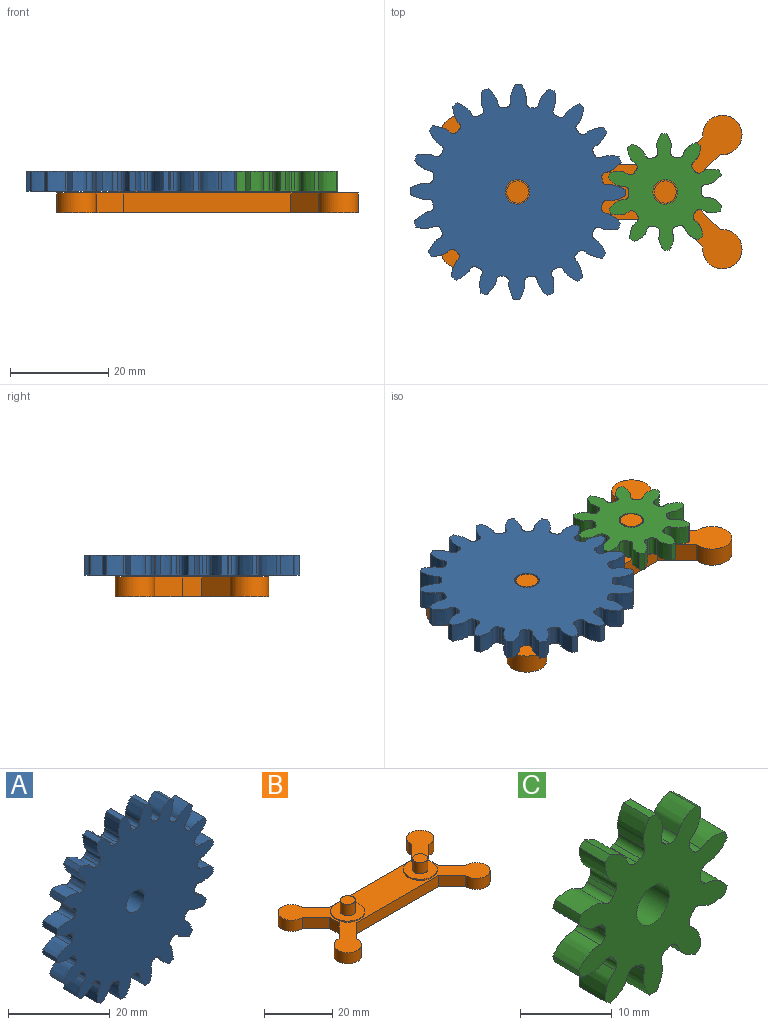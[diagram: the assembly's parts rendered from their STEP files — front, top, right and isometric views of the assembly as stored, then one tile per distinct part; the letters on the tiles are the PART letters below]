
ASSEMBLY  parts=3 mates=2
PART A: 123 faces, bbox 43.9x4.5x43.9 mm
  f0: cylinder r=21.88mm len=4mm, axis (0,1,0), area 5mm2, adj f19,f22,f73,f120
  f1: cylinder r=21.88mm len=4mm, axis (0,1,0), area 5mm2, adj f19,f22,f115,f118
  f2: cylinder r=21.88mm len=4mm, axis (0,1,0), area 5mm2, adj f19,f22,f110,f113
  f3: cylinder r=21.88mm len=4mm, axis (0,1,0), area 5mm2, adj f19,f22,f105,f108
  f4: cylinder r=21.88mm len=4mm, axis (0,1,0), area 5mm2, adj f19,f22,f100,f103
  f5: cylinder r=21.88mm len=4mm, axis (0,1,0), area 5mm2, adj f19,f22,f95,f98
  f6: cylinder r=21.88mm len=4mm, axis (0,1,0), area 5mm2, adj f19,f22,f90,f93
  f7: cylinder r=21.88mm len=4mm, axis (0,1,0), area 5mm2, adj f19,f22,f85,f88
  f8: cylinder r=21.88mm len=4mm, axis (0,1,0), area 5mm2, adj f19,f22,f68,f80
  f9: cylinder r=21.88mm len=4mm, axis (0,1,0), area 5mm2, adj f19,f22,f75,f78
  f10: cylinder r=21.88mm len=4mm, axis (0,1,0), area 5mm2, adj f19,f22,f63,f70
  f11: cylinder r=21.88mm len=4mm, axis (0,1,0), area 5mm2, adj f19,f22,f43,f65
  f12: cylinder r=21.88mm len=4mm, axis (0,1,0), area 5mm2, adj f19,f22,f23,f60
  f13: cylinder r=21.88mm len=4mm, axis (0,1,0), area 5mm2, adj f19,f22,f55,f58
  f14: cylinder r=21.88mm len=4mm, axis (0,1,0), area 5mm2, adj f19,f22,f50,f53
  f15: cylinder r=21.88mm len=4mm, axis (0,1,0), area 5mm2, adj f19,f22,f45,f48
  f16: cylinder r=21.88mm len=4mm, axis (0,1,0), area 5mm2, adj f19,f22,f33,f40
  f17: cylinder r=21.88mm len=4mm, axis (0,1,0), area 5mm2, adj f19,f22,f35,f83
  f18: cylinder r=21.88mm len=4mm, axis (0,1,0), area 5mm2, adj f19,f22,f30,f38
  f19: plane 43.87x43.87mm, normal (0,-1,0), area 1180.5mm2, adj f0,f1,f2,f3,f4,f5,f6,f7
  f20: cylinder r=2.5mm len=5mm, axis (0,1,0), area 62.8mm2, adj f19,f22
  f21: cylinder r=21.88mm len=4mm, axis (0,1,0), area 5mm2, adj f19,f22,f25,f28
  f22: plane 43.87x43.87mm, normal (0,1,0), area 1180.5mm2, adj f0,f1,f2,f3,f4,f5,f6,f7
  f23: extruded ~4x3.46mm, area 15.4mm2, adj f12,f19,f22,f26
  f24: cylinder r=17.38mm len=4mm, axis (0,1,0), area 2.8mm2, adj f19,f22,f26,f27
  f25: extruded ~4x3.46mm, area 15.4mm2, adj f19,f21,f22,f27
  f26: cylinder r=0.92mm len=4mm, axis (0,1,0), area 5.6mm2, adj f19,f22,f23,f24
  f27: cylinder r=0.92mm len=4mm, axis (0,1,0), area 5.6mm2, adj f19,f22,f24,f25
  f28: extruded ~4x3.77mm, area 15.4mm2, adj f19,f21,f22,f31
  f29: cylinder r=17.38mm len=4mm, axis (0,1,0), area 2.8mm2, adj f19,f22,f31,f32
  f30: extruded ~4x2.82mm, area 15.4mm2, adj f18,f19,f22,f32
  f31: cylinder r=0.92mm len=4mm, axis (0,1,0), area 5.6mm2, adj f19,f22,f28,f29
  f32: cylinder r=0.92mm len=4mm, axis (0,1,0), area 5.6mm2, adj f19,f22,f29,f30
  f33: extruded ~4x3.27mm, area 15.4mm2, adj f16,f19,f22,f36
  f34: cylinder r=17.38mm len=4mm, axis (0,1,0), area 2.8mm2, adj f19,f22,f36,f37
  f35: extruded ~4x3.7mm, area 15.4mm2, adj f17,f19,f22,f37
  f36: cylinder r=0.92mm len=4mm, axis (0,1,0), area 5.6mm2, adj f19,f22,f33,f34
  f37: cylinder r=0.92mm len=4mm, axis (0,1,0), area 5.6mm2, adj f19,f22,f34,f35
  f38: extruded ~4x3.7mm, area 15.4mm2, adj f18,f19,f22,f41
  f39: cylinder r=17.38mm len=4mm, axis (0,1,0), area 2.8mm2, adj f19,f22,f41,f42
  f40: extruded ~4x3.27mm, area 15.4mm2, adj f16,f19,f22,f42
  f41: cylinder r=0.92mm len=4mm, axis (0,1,0), area 5.6mm2, adj f19,f22,f38,f39
  f42: cylinder r=0.92mm len=4mm, axis (0,1,0), area 5.6mm2, adj f19,f22,f39,f40
  f43: extruded ~4x3.77mm, area 15.4mm2, adj f11,f19,f22,f46
  f44: cylinder r=17.38mm len=4mm, axis (0,1,0), area 2.8mm2, adj f19,f22,f46,f47
  f45: extruded ~4x2.82mm, area 15.4mm2, adj f15,f19,f22,f47
  f46: cylinder r=0.92mm len=4mm, axis (0,1,0), area 5.6mm2, adj f19,f22,f43,f44
  f47: cylinder r=0.92mm len=4mm, axis (0,1,0), area 5.6mm2, adj f19,f22,f44,f45
  f48: extruded ~4x3.7mm, area 15.4mm2, adj f15,f19,f22,f51
  f49: cylinder r=17.38mm len=4mm, axis (0,1,0), area 2.8mm2, adj f19,f22,f51,f52
  f50: extruded ~4x3.27mm, area 15.4mm2, adj f14,f19,f22,f52
  f51: cylinder r=0.92mm len=4mm, axis (0,1,0), area 5.6mm2, adj f19,f22,f48,f49
  f52: cylinder r=0.92mm len=4mm, axis (0,1,0), area 5.6mm2, adj f19,f22,f49,f50
  f53: extruded ~4x3.27mm, area 15.4mm2, adj f14,f19,f22,f56
  f54: cylinder r=17.38mm len=4mm, axis (0,1,0), area 2.8mm2, adj f19,f22,f56,f57
  f55: extruded ~4x3.7mm, area 15.4mm2, adj f13,f19,f22,f57
  f56: cylinder r=0.92mm len=4mm, axis (0,1,0), area 5.6mm2, adj f19,f22,f53,f54
  f57: cylinder r=0.92mm len=4mm, axis (0,1,0), area 5.6mm2, adj f19,f22,f54,f55
  f58: extruded ~4x2.82mm, area 15.4mm2, adj f13,f19,f22,f61
  f59: cylinder r=17.38mm len=4mm, axis (0,1,0), area 2.8mm2, adj f19,f22,f61,f62
  f60: extruded ~4x3.77mm, area 15.4mm2, adj f12,f19,f22,f62
  f61: cylinder r=0.92mm len=4mm, axis (0,1,0), area 5.6mm2, adj f19,f22,f58,f59
  f62: cylinder r=0.92mm len=4mm, axis (0,1,0), area 5.6mm2, adj f19,f22,f59,f60
  f63: extruded ~4x3.46mm, area 15.4mm2, adj f10,f19,f22,f66
  f64: cylinder r=17.38mm len=4mm, axis (0,1,0), area 2.8mm2, adj f19,f22,f66,f67
  f65: extruded ~4x3.46mm, area 15.4mm2, adj f11,f19,f22,f67
  f66: cylinder r=0.92mm len=4mm, axis (0,1,0), area 5.6mm2, adj f19,f22,f63,f64
  f67: cylinder r=0.92mm len=4mm, axis (0,1,0), area 5.6mm2, adj f19,f22,f64,f65
  f68: extruded ~4x2.82mm, area 15.4mm2, adj f8,f19,f22,f71
  f69: cylinder r=17.38mm len=4mm, axis (0,1,0), area 2.8mm2, adj f19,f22,f71,f72
  f70: extruded ~4x3.77mm, area 15.4mm2, adj f10,f19,f22,f72
  f71: cylinder r=0.92mm len=4mm, axis (0,1,0), area 5.6mm2, adj f19,f22,f68,f69
  f72: cylinder r=0.92mm len=4mm, axis (0,1,0), area 5.6mm2, adj f19,f22,f69,f70
  f73: extruded ~4x3.7mm, area 15.4mm2, adj f0,f19,f22,f76
  f74: cylinder r=17.38mm len=4mm, axis (0,1,0), area 2.8mm2, adj f19,f22,f76,f77
  f75: extruded ~4x3.27mm, area 15.4mm2, adj f9,f19,f22,f77
  f76: cylinder r=0.92mm len=4mm, axis (0,1,0), area 5.6mm2, adj f19,f22,f73,f74
  f77: cylinder r=0.92mm len=4mm, axis (0,1,0), area 5.6mm2, adj f19,f22,f74,f75
  f78: extruded ~4x3.27mm, area 15.4mm2, adj f9,f19,f22,f81
  f79: cylinder r=17.38mm len=4mm, axis (0,1,0), area 2.8mm2, adj f19,f22,f81,f82
  f80: extruded ~4x3.7mm, area 15.4mm2, adj f8,f19,f22,f82
  f81: cylinder r=0.92mm len=4mm, axis (0,1,0), area 5.6mm2, adj f19,f22,f78,f79
  f82: cylinder r=0.92mm len=4mm, axis (0,1,0), area 5.6mm2, adj f19,f22,f79,f80
  f83: extruded ~4x2.82mm, area 15.4mm2, adj f17,f19,f22,f86
  f84: cylinder r=17.38mm len=4mm, axis (0,1,0), area 2.8mm2, adj f19,f22,f86,f87
  f85: extruded ~4x3.77mm, area 15.4mm2, adj f7,f19,f22,f87
  f86: cylinder r=0.92mm len=4mm, axis (0,1,0), area 5.6mm2, adj f19,f22,f83,f84
  f87: cylinder r=0.92mm len=4mm, axis (0,1,0), area 5.6mm2, adj f19,f22,f84,f85
  f88: extruded ~4x3.46mm, area 15.4mm2, adj f7,f19,f22,f91
  f89: cylinder r=17.38mm len=4mm, axis (0,1,0), area 2.8mm2, adj f19,f22,f91,f92
  f90: extruded ~4x3.46mm, area 15.4mm2, adj f6,f19,f22,f92
  f91: cylinder r=0.92mm len=4mm, axis (0,1,0), area 5.6mm2, adj f19,f22,f88,f89
  f92: cylinder r=0.92mm len=4mm, axis (0,1,0), area 5.6mm2, adj f19,f22,f89,f90
  f93: extruded ~4x3.77mm, area 15.4mm2, adj f6,f19,f22,f96
  f94: cylinder r=17.38mm len=4mm, axis (0,1,0), area 2.8mm2, adj f19,f22,f96,f97
  f95: extruded ~4x2.82mm, area 15.4mm2, adj f5,f19,f22,f97
  f96: cylinder r=0.92mm len=4mm, axis (0,1,0), area 5.6mm2, adj f19,f22,f93,f94
  f97: cylinder r=0.92mm len=4mm, axis (0,1,0), area 5.6mm2, adj f19,f22,f94,f95
  f98: extruded ~4x3.7mm, area 15.4mm2, adj f5,f19,f22,f101
  f99: cylinder r=17.38mm len=4mm, axis (0,1,0), area 2.8mm2, adj f19,f22,f101,f102
  f100: extruded ~4x3.27mm, area 15.4mm2, adj f4,f19,f22,f102
  f101: cylinder r=0.92mm len=4mm, axis (0,1,0), area 5.6mm2, adj f19,f22,f98,f99
  f102: cylinder r=0.92mm len=4mm, axis (0,1,0), area 5.6mm2, adj f19,f22,f99,f100
  f103: extruded ~4x3.27mm, area 15.4mm2, adj f4,f19,f22,f106
  f104: cylinder r=17.38mm len=4mm, axis (0,1,0), area 2.8mm2, adj f19,f22,f106,f107
  f105: extruded ~4x3.7mm, area 15.4mm2, adj f3,f19,f22,f107
  f106: cylinder r=0.92mm len=4mm, axis (0,1,0), area 5.6mm2, adj f19,f22,f103,f104
  f107: cylinder r=0.92mm len=4mm, axis (0,1,0), area 5.6mm2, adj f19,f22,f104,f105
  f108: extruded ~4x2.82mm, area 15.4mm2, adj f3,f19,f22,f111
  f109: cylinder r=17.38mm len=4mm, axis (0,1,0), area 2.8mm2, adj f19,f22,f111,f112
  f110: extruded ~4x3.77mm, area 15.4mm2, adj f2,f19,f22,f112
  f111: cylinder r=0.92mm len=4mm, axis (0,1,0), area 5.6mm2, adj f19,f22,f108,f109
  f112: cylinder r=0.92mm len=4mm, axis (0,1,0), area 5.6mm2, adj f19,f22,f109,f110
  f113: extruded ~4x3.46mm, area 15.4mm2, adj f2,f19,f22,f116
  f114: cylinder r=17.38mm len=4mm, axis (0,1,0), area 2.8mm2, adj f19,f22,f116,f117
  f115: extruded ~4x3.46mm, area 15.4mm2, adj f1,f19,f22,f117
  f116: cylinder r=0.92mm len=4mm, axis (0,1,0), area 5.6mm2, adj f19,f22,f113,f114
  f117: cylinder r=0.92mm len=4mm, axis (0,1,0), area 5.6mm2, adj f19,f22,f114,f115
  f118: extruded ~4x3.77mm, area 15.4mm2, adj f1,f19,f22,f121
  f119: cylinder r=17.38mm len=4mm, axis (0,1,0), area 2.8mm2, adj f19,f22,f121,f122
  f120: extruded ~4x2.82mm, area 15.4mm2, adj f0,f19,f22,f122
  f121: cylinder r=0.92mm len=4mm, axis (0,1,0), area 5.6mm2, adj f19,f22,f118,f119
  f122: cylinder r=0.92mm len=4mm, axis (0,1,0), area 5.6mm2, adj f19,f22,f119,f120
PART B: 26 faces, bbox 61.3x31.2x8.4 mm
  f0: cylinder r=4mm len=8mm, axis (0,0,1), area 78.9mm2, adj f1,f15,f16,f17
  f1: plane 5.66x5.66mm, normal (-0.71,0.71,0), area 32mm2, adj f0,f2,f16,f17
  f2: plane 34x4mm, normal (0,1,0), area 136mm2, adj f1,f3,f16,f17
  f3: plane 5.66x5.66mm, normal (0.71,0.71,0), area 32mm2, adj f2,f4,f16,f17
  f4: cylinder r=4mm len=8mm, axis (0,0,1), area 78.9mm2, adj f3,f5,f16,f17
  f5: plane 5.66x5.66mm, normal (-0.71,-0.71,0), area 32mm2, adj f4,f6,f16,f17
  f6: plane 4x3.93mm, normal (-1,0,0), area 15.7mm2, adj f5,f7,f16,f17
  f7: plane 5.66x5.66mm, normal (-0.71,0.71,0), area 32mm2, adj f6,f8,f16,f17
  f8: cylinder r=4mm len=8mm, axis (0,0,1), area 78.9mm2, adj f7,f9,f16,f17
  f9: plane 5.66x5.66mm, normal (0.71,-0.71,0), area 32mm2, adj f8,f10,f16,f17
  f10: plane 34x4mm, normal (0,-1,0), area 136mm2, adj f9,f11,f16,f17
  f11: plane 5.66x5.66mm, normal (-0.71,-0.71,0), area 32mm2, adj f10,f12,f16,f17
  f12: cylinder r=4mm len=8mm, axis (0,0,1), area 78.9mm2, adj f11,f13,f16,f17
  f13: plane 5.66x5.66mm, normal (0.71,0.71,0), area 32mm2, adj f12,f14,f16,f17
  f14: plane 4x3.93mm, normal (1,0,0), area 15.7mm2, adj f13,f15,f16,f17
  f15: plane 5.66x5.66mm, normal (0.71,-0.71,0), area 32mm2, adj f0,f14,f16,f17
  f16: plane 61.27x31.19mm, normal (0,0,-1), area 775.9mm2, adj f0,f1,f2,f3,f4,f5,f6,f7
  f17: plane 61.27x31.19mm, normal (0,0,1), area 618.8mm2, adj f0,f1,f2,f3,f4,f5,f6,f7
  f18: cylinder r=5mm len=10mm, axis (0,0,-1), area 12.6mm2, adj f17,f19
  f19: plane 10x10mm, normal (0,0,1), area 62.6mm2, adj f18,f21
  f20: plane 4.5x4.5mm, normal (0,0,1), area 15.9mm2, adj f21
  f21: cylinder r=2.25mm len=4.5mm, axis (0,0,-1), area 56.5mm2, adj f19,f20
  f22: cylinder r=5mm len=10mm, axis (0,0,-1), area 12.6mm2, adj f17,f23
  f23: plane 10x10mm, normal (0,0,1), area 62.6mm2, adj f22,f25
  f24: plane 4.5x4.5mm, normal (0,0,1), area 15.9mm2, adj f25
  f25: cylinder r=2.25mm len=4.5mm, axis (0,0,-1), area 56.5mm2, adj f23,f24
PART C: 63 faces, bbox 24.1x5.2x24.9 mm
  f0: cylinder r=11.88mm len=4mm, axis (0,1,0), area 4.2mm2, adj f9,f12,f53,f60
  f1: cylinder r=11.88mm len=4mm, axis (0,1,0), area 4.2mm2, adj f9,f12,f13,f55
  f2: cylinder r=11.88mm len=4mm, axis (0,1,0), area 4.2mm2, adj f9,f12,f43,f50
  f3: cylinder r=11.88mm len=4mm, axis (0,1,0), area 4.2mm2, adj f9,f12,f45,f58
  f4: cylinder r=11.88mm len=4mm, axis (0,1,0), area 4.2mm2, adj f9,f12,f33,f40
  f5: cylinder r=11.88mm len=4mm, axis (0,1,0), area 4.2mm2, adj f9,f12,f28,f35
  f6: cylinder r=11.88mm len=4mm, axis (0,1,0), area 4.2mm2, adj f9,f12,f23,f30
  f7: cylinder r=11.88mm len=4mm, axis (0,1,0), area 4.2mm2, adj f9,f12,f25,f48
  f8: cylinder r=11.88mm len=4mm, axis (0,1,0), area 4.2mm2, adj f9,f12,f20,f38
  f9: plane 24.94x24.08mm, normal (0,-1,0), area 265.5mm2, adj f0,f1,f2,f3,f4,f5,f6,f7
  f10: cylinder r=2.5mm len=5mm, axis (0,1,0), area 62.8mm2, adj f9,f12
  f11: cylinder r=11.88mm len=4mm, axis (0,1,0), area 4.2mm2, adj f9,f12,f15,f18
  f12: plane 24.94x24.08mm, normal (0,1,0), area 265.5mm2, adj f0,f1,f2,f3,f4,f5,f6,f7
  f13: extruded ~4x3.26mm, area 15.6mm2, adj f1,f9,f12,f16
  f14: cylinder r=7.38mm len=4mm, axis (0,1,0), area 2.5mm2, adj f9,f12,f16,f17
  f15: extruded ~4x3.26mm, area 15.6mm2, adj f9,f11,f12,f17
  f16: cylinder r=0.95mm len=4mm, axis (0,1,0), area 5.6mm2, adj f9,f12,f13,f14
  f17: cylinder r=0.95mm len=4mm, axis (0,1,0), area 5.6mm2, adj f9,f12,f14,f15
  f18: extruded ~4x3.74mm, area 15.6mm2, adj f9,f11,f12,f21
  f19: cylinder r=7.38mm len=4mm, axis (0,1,0), area 2.5mm2, adj f9,f12,f21,f22
  f20: extruded ~4x3.43mm, area 15.6mm2, adj f8,f9,f12,f22
  f21: cylinder r=0.95mm len=4mm, axis (0,1,0), area 5.6mm2, adj f9,f12,f18,f19
  f22: cylinder r=0.95mm len=4mm, axis (0,1,0), area 5.6mm2, adj f9,f12,f19,f20
  f23: extruded ~4x3.26mm, area 15.6mm2, adj f6,f9,f12,f26
  f24: cylinder r=7.38mm len=4mm, axis (0,1,0), area 2.5mm2, adj f9,f12,f26,f27
  f25: extruded ~4x3.26mm, area 15.6mm2, adj f7,f9,f12,f27
  f26: cylinder r=0.95mm len=4mm, axis (0,1,0), area 5.6mm2, adj f9,f12,f23,f24
  f27: cylinder r=0.95mm len=4mm, axis (0,1,0), area 5.6mm2, adj f9,f12,f24,f25
  f28: extruded ~4x3.43mm, area 15.6mm2, adj f5,f9,f12,f31
  f29: cylinder r=7.38mm len=4mm, axis (0,1,0), area 2.5mm2, adj f9,f12,f31,f32
  f30: extruded ~4x3.74mm, area 15.6mm2, adj f6,f9,f12,f32
  f31: cylinder r=0.95mm len=4mm, axis (0,1,0), area 5.6mm2, adj f9,f12,f28,f29
  f32: cylinder r=0.95mm len=4mm, axis (0,1,0), area 5.6mm2, adj f9,f12,f29,f30
  f33: extruded ~4x3.68mm, area 15.6mm2, adj f4,f9,f12,f36
  f34: cylinder r=7.38mm len=4mm, axis (0,1,0), area 2.5mm2, adj f9,f12,f36,f37
  f35: extruded ~4x2.79mm, area 15.6mm2, adj f5,f9,f12,f37
  f36: cylinder r=0.95mm len=4mm, axis (0,1,0), area 5.6mm2, adj f9,f12,f33,f34
  f37: cylinder r=0.95mm len=4mm, axis (0,1,0), area 5.6mm2, adj f9,f12,f34,f35
  f38: extruded ~4x2.79mm, area 15.6mm2, adj f8,f9,f12,f41
  f39: cylinder r=7.38mm len=4mm, axis (0,1,0), area 2.5mm2, adj f9,f12,f41,f42
  f40: extruded ~4x3.68mm, area 15.6mm2, adj f4,f9,f12,f42
  f41: cylinder r=0.95mm len=4mm, axis (0,1,0), area 5.6mm2, adj f9,f12,f38,f39
  f42: cylinder r=0.95mm len=4mm, axis (0,1,0), area 5.6mm2, adj f9,f12,f39,f40
  f43: extruded ~4x2.79mm, area 15.6mm2, adj f2,f9,f12,f46
  f44: cylinder r=7.38mm len=4mm, axis (0,1,0), area 2.5mm2, adj f9,f12,f46,f47
  f45: extruded ~4x3.68mm, area 15.6mm2, adj f3,f9,f12,f47
  f46: cylinder r=0.95mm len=4mm, axis (0,1,0), area 5.6mm2, adj f9,f12,f43,f44
  f47: cylinder r=0.95mm len=4mm, axis (0,1,0), area 5.6mm2, adj f9,f12,f44,f45
  f48: extruded ~4x3.74mm, area 15.6mm2, adj f7,f9,f12,f51
  f49: cylinder r=7.38mm len=4mm, axis (0,1,0), area 2.5mm2, adj f9,f12,f51,f52
  f50: extruded ~4x3.43mm, area 15.6mm2, adj f2,f9,f12,f52
  f51: cylinder r=0.95mm len=4mm, axis (0,1,0), area 5.6mm2, adj f9,f12,f48,f49
  f52: cylinder r=0.95mm len=4mm, axis (0,1,0), area 5.6mm2, adj f9,f12,f49,f50
  f53: extruded ~4x3.43mm, area 15.6mm2, adj f0,f9,f12,f56
  f54: cylinder r=7.38mm len=4mm, axis (0,1,0), area 2.5mm2, adj f9,f12,f56,f57
  f55: extruded ~4x3.74mm, area 15.6mm2, adj f1,f9,f12,f57
  f56: cylinder r=0.95mm len=4mm, axis (0,1,0), area 5.6mm2, adj f9,f12,f53,f54
  f57: cylinder r=0.95mm len=4mm, axis (0,1,0), area 5.6mm2, adj f9,f12,f54,f55
  f58: extruded ~4x3.68mm, area 15.6mm2, adj f3,f9,f12,f61
  f59: cylinder r=7.38mm len=4mm, axis (0,1,0), area 2.5mm2, adj f9,f12,f61,f62
  f60: extruded ~4x2.79mm, area 15.6mm2, adj f0,f9,f12,f62
  f61: cylinder r=0.95mm len=4mm, axis (0,1,0), area 5.6mm2, adj f9,f12,f58,f59
  f62: cylinder r=0.95mm len=4mm, axis (0,1,0), area 5.6mm2, adj f9,f12,f59,f60
PLACE A rot(axis=(-0.64,-0.54,0.54),114.7deg) t=(-15,0,4.4)mm
PLACE B t=(0,0,4)mm
PLACE C rot(axis=(-0.92,0.28,-0.28),95.1deg) t=(15,0,4.4)mm
MATE revolute A.f0 <-> B.f21  axis (0,0,1) through (-15,0,8.4)mm
MATE revolute C.f0 <-> B.f25  axis (0,0,1) through (15,0,8.4)mm
